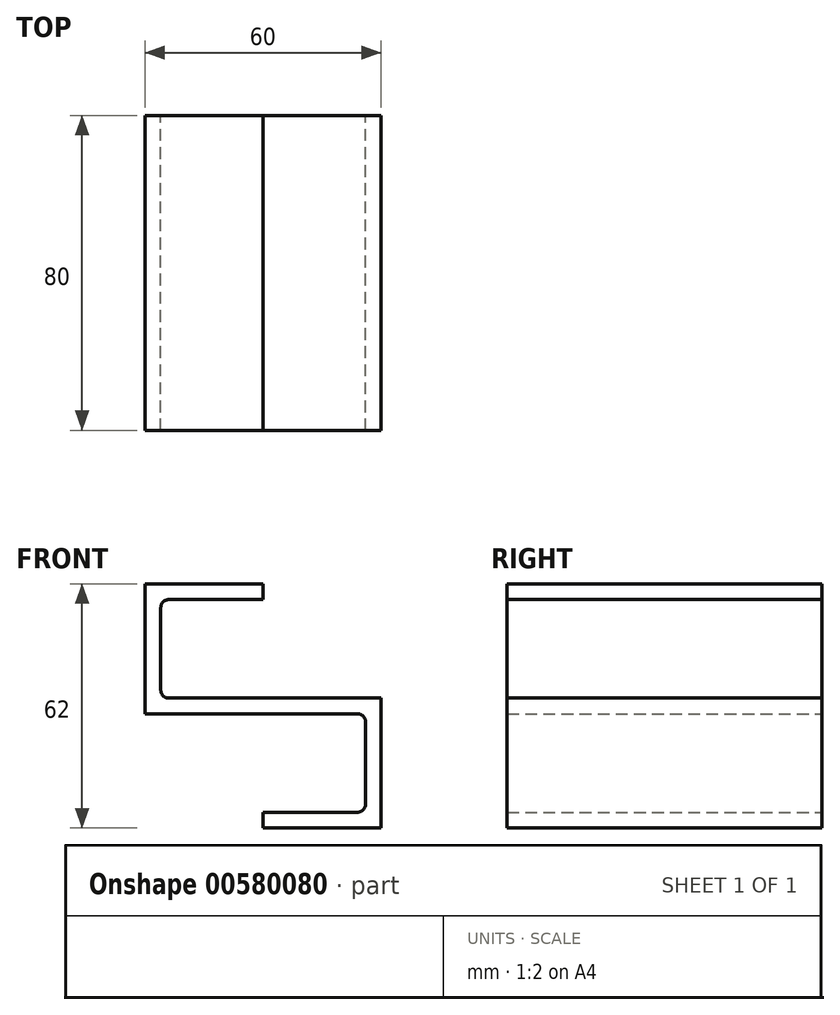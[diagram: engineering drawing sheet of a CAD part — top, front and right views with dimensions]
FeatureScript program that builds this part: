
annotation { "Feature Type Name" : "Feature", "Feature Type Description" : "" }
export const myFeature = defineFeature(function(context is Context, id is Id, definition is map)
    precondition{}
    {
        {
            var Q0;
            Q0=qCreatedBy(makeId("Front.planeOp"),FACE);
            var sketch = newSketch(context, id + "F0", { "sketchPlane" : qUnion([Q0])});
            skLineSegment(sketch, "E0", {"start": v(0, 0) * mm, "end": v(24, 0) * mm});
            skLineSegment(sketch, "E1", {"start": v(26, 2) * mm, "end": v(26, 23) * mm});
            skLineSegment(sketch, "E2", {"start": v(24, 25) * mm, "end": v(-30, 25) * mm});
            skLineSegment(sketch, "E3", {"start": v(-30, 25) * mm, "end": v(-30, 58) * mm});
            skLineSegment(sketch, "E4", {"start": v(-30, 58) * mm, "end": v(0, 58) * mm});
            skLineSegment(sketch, "E5.0", {"start": v(-24, 54) * mm, "end": v(0, 54) * mm});
            skLineSegment(sketch, "E5.1", {"start": v(0, -4) * mm, "end": v(30, -4) * mm});
            skLineSegment(sketch, "E5.2", {"start": v(30, -4) * mm, "end": v(30, 29) * mm});
            skLineSegment(sketch, "E5.3", {"start": v(30, 29) * mm, "end": v(-24, 29) * mm});
            skLineSegment(sketch, "E5.4", {"start": v(-26, 31) * mm, "end": v(-26, 52) * mm});
            skLineSegment(sketch, "E6", {"start": v(0, 54) * mm, "end": v(0, 58) * mm});
            skLineSegment(sketch, "E7", {"start": v(0, 0) * mm, "end": v(0, -4) * mm});
            skPoint(sketch, "E8.visualSharp", {"position": v(-26, 54) * mm});
            skArc(sketch, "E8.filletArc", {"start": v(-24, 54) * mm, "mid": v(-25.41, 53.41) * mm, "end": v(-26, 52) * mm});
            skPoint(sketch, "E9.visualSharp", {"position": v(-26, 29) * mm});
            skArc(sketch, "E9.filletArc", {"start": v(-26, 31) * mm, "mid": v(-25.41, 29.59) * mm, "end": v(-24, 29) * mm});
            skPoint(sketch, "E10.visualSharp", {"position": v(26, 25) * mm});
            skArc(sketch, "E10.filletArc", {"start": v(26, 23) * mm, "mid": v(25.41, 24.41) * mm, "end": v(24, 25) * mm});
            skPoint(sketch, "E11.visualSharp", {"position": v(26, 0) * mm});
            skArc(sketch, "E11.filletArc", {"start": v(24, 0) * mm, "mid": v(25.41, 0.59) * mm, "end": v(26, 2) * mm});
            skSolve(sketch);
        }
        {
            var Q0;
            Q0 = qSketchRegion(id + "F0", true);
            extrude(context, id + "F1", {"entities" : qUnion([Q0]), "depth" : 80 * mm, "offsetDistance" : 25 * mm});
        }
    });
